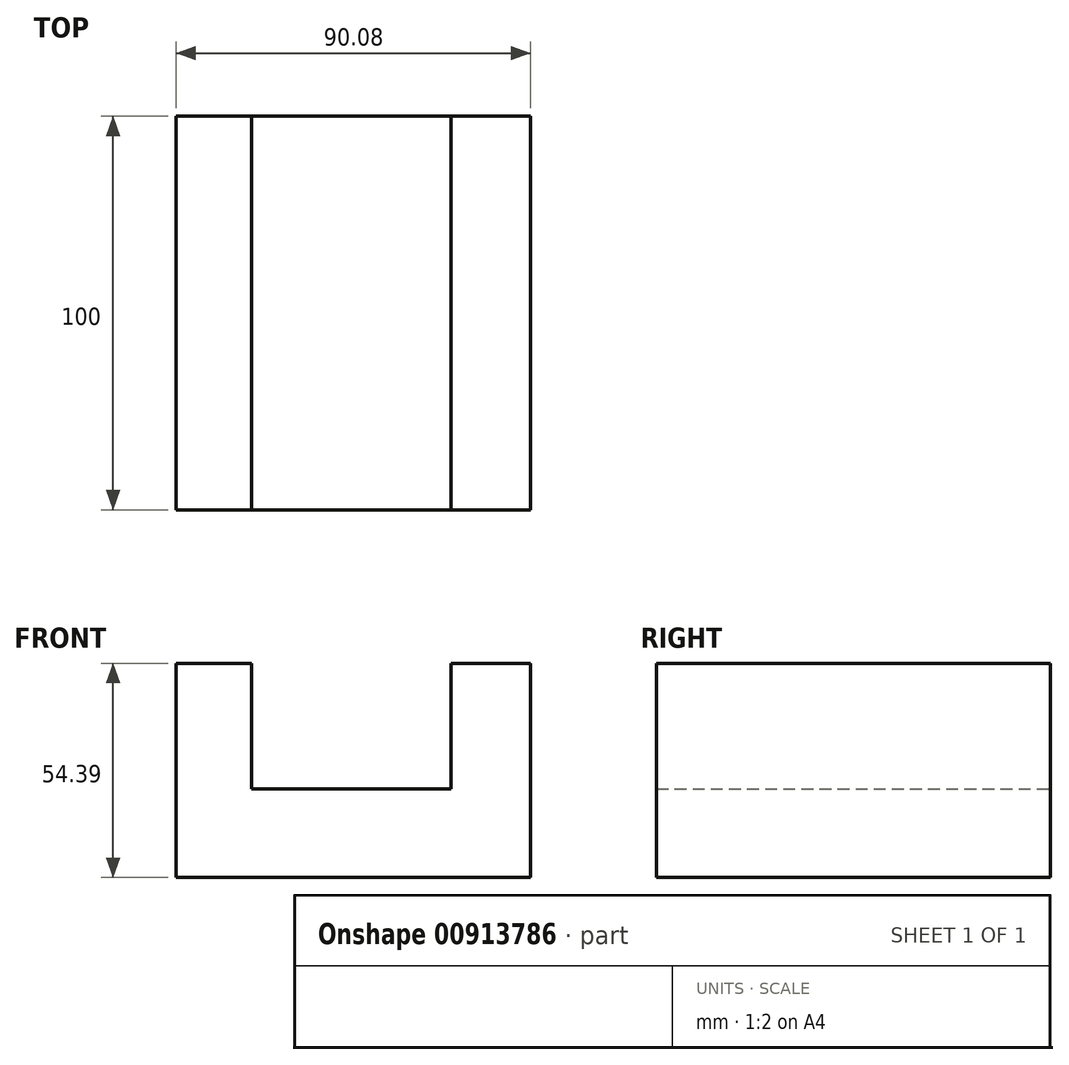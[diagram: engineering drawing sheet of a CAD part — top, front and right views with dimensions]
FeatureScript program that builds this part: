
annotation { "Feature Type Name" : "Feature", "Feature Type Description" : "" }
export const myFeature = defineFeature(function(context is Context, id is Id, definition is map)
    precondition{}
    {
        {
            var Q0;
            Q0=qCreatedBy(makeId("Front.planeOp"),FACE);
            var sketch = newSketch(context, id + "F0", { "sketchPlane" : qUnion([Q0])});
            skLineSegment(sketch, "E0.bottom", {"start": v(-49.48, 19.75) * mm, "end": v(-30.23, 19.75) * mm});
            skLineSegment(sketch, "E0.top", {"start": v(-49.48, -34.64) * mm, "end": v(40.6, -34.64) * mm});
            skLineSegment(sketch, "E0.left", {"start": v(-49.48, 19.75) * mm, "end": v(-49.48, -34.64) * mm});
            skLineSegment(sketch, "E0.right", {"start": v(40.6, 19.75) * mm, "end": v(40.6, -34.64) * mm});
            skLineSegment(sketch, "E1.top", {"start": v(-30.23, -12.13) * mm, "end": v(20.36, -12.13) * mm});
            skLineSegment(sketch, "E1.left", {"start": v(-30.23, 19.75) * mm, "end": v(-30.23, -12.13) * mm});
            skLineSegment(sketch, "E1.right", {"start": v(20.36, 19.75) * mm, "end": v(20.36, -12.13) * mm});
            skLineSegment(sketch, "E2.trimOffspring", {"start": v(20.36, 19.75) * mm, "end": v(40.6, 19.75) * mm});
            skSolve(sketch);
        }
        {
            var Q0;
            Q0=makeQuery(id+"F0.imprint","IMPRINT",FACE,{"disambiguationData":[TD([[makeQuery(id+"F0.imprint","IMPRINT",EDGE,{"derivedFrom":sQuery(id+"F0.wireOp",EDGE,"E0.bottom")}),-1.0]])]});
            extrude(context, id + "F1", {"entities" : qUnion([Q0]), "depth" : 50 * mm, "offsetDistance" : 25.4 * mm, "hasSecondDirection" : true, "secondDirectionOppositeDirection" : true, "secondDirectionDepth" : 50 * mm});
        }
    });
